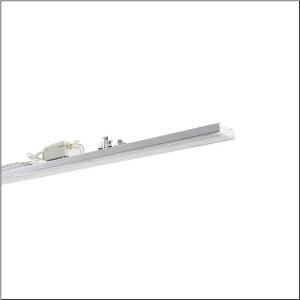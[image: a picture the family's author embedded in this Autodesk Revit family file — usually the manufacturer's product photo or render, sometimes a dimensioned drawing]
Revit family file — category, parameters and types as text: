
# Revit family: licross_r__21_recessed_mo_52te12dv4fxg_0884
name_source: partatom
category: Lighting Fixtures
units: mm (PartAtom-declared; Revit-internal decimal feet)

## family parameters
Cut with Voids When Loaded = No
Host = Face
Light Source = No
Part Type = Normal
Room Calculation Point = No
Round Connector Dimension = Use Diameter
Shared = No

## types (1)
- --- (1 x LED, 15420 lm, 85.3 W, 4000K)
    Apparent Load = 85 VA
    CIE Flux Codes = 72 92 99 100 100
    Color Rendering = 80
    Color Temperature = 4000K
    Default Elevation = 1800 mm
    Description = Licross® 21 Recessed MO, luminaire insert, of sheet steel, galvanised, coil coated, white, length: 2.250mm, width: 66mm, height: 67mm, LED rated luminous flux: 15.420lm, light colour: 840, control gear: DALI 2, with plug, 5-pole, with phase selection, mains connection: 220..240V, AC, 50/60Hz, rated input power: 85W, halogen-free wiring, primary optical cover: cover, of PMMA, light emission: direct distribution, primary light characteristic: symmetric, protection rating (complete): IP54, insulation class (complete): insulation class I (protective earthing), certification: CE, ENEC, VDE, UKCA, protection symbol: D if used in an environment with non-conductive dust loads with corresponding accessories, impact resistance: IK06, permissible ambient temperature for indoor applications: -25..+35°C, corresponds to IFS (International Featured Standards) requirements for safety and quality in the food industry, reducing of maximum allowable ambient temperature of 5°C with ceiling mounting, LABS conformity tested according to VDMA 24364:2018-05, packaging unit: 1 piece
    Height = 58 mm
    Lamp = 1 x LED
    Lamp Light Flux = 15420 lm
    Lamp Power = 85.3 W
    Lamp count = 1
    Length = 2250 mm
    Luminous efficacy = 181 lm/W
    Manufacturer = Siteco
    ModVariant = No
    Model = 52TE12DV4FXG
    Mounting Place = Ceiling
    Mounting Type = Pendant
    Number of Poles = 1
    OnlyDefault = Yes
    Power Factor = 1
    Product Name = Licross® 21 Recessed MO
    Product group = luminaire insert
    ProductGroupID = 901
    Protection Class = Protection class I
    Protection Degree = IP 54
    RLX_Detail_Level = 1
    RLX_Emergency_Light_Flux = 0 lm
    RLX_Emergency_Type = 0
    RLX_Emergency_Type_DB = No
    RlxData = <blob elided: 29425 chars, md5=216be60a>
    Socket = socket
    Standby Power = 0 W
    System Light Flux = 15420 lm
    System Power = 85 W
    Type Comments = factory setting: luminous flux: 100 % | dim-lin: 254 | 390 mA
    Type Image = l_1296930.jpg
    URL = http://relux.com
    VarID = @adj_057947
    Voltage = 0 V
    Weight = 0.00 kg
    Width = 66 mm

## geometry (parser evidence)
native form markers: Blend x4, Sweep x11
no freeform markers — native parametric forms only
